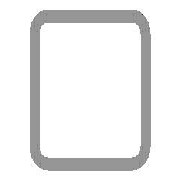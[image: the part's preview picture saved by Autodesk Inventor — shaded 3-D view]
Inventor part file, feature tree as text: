
AUTODESK INVENTOR PART (.ipt)
format: ipt  version: 2018 (Build 220112000, 112)  size: 129,536 bytes
history: native  units: mm (DEFAULTED — no unit token found)
features: other x3, sketch x3, extrude x1, plane x1
ambient origin geometry x8: Origin, YZ Plane, XZ Plane, XY Plane, X Axis, Y Axis, Z Axis, Center Point
bodies: Solid1 (feature_tree)
feature tree (8):
  other  "Driven Length"
  other  "Piano iniziale"
  other  "Piano finale"
  extrude  "Corpo"  TaperAngle=0.0deg  [1 undecoded]
  sketch  "Schizzo"
  sketch  "Sketch3"  dims[d3=370.0mm d4=0.0mm]
  plane  "Work Plane3"
  sketch  "Sketch4"  dims[d7=4.0mm d9=40.0mm d11=40.0mm d12=2.0mm d13=-0.0mm d14=370.0mm d15=20.0mm d16=20.0mm d17=90.0deg d18=370.0mm]
note: 1 required parameter value undecoded (feature->parameter linkage not recoverable at this tier; creation-order binding heuristic only, values carry confidence <= 0.55)
